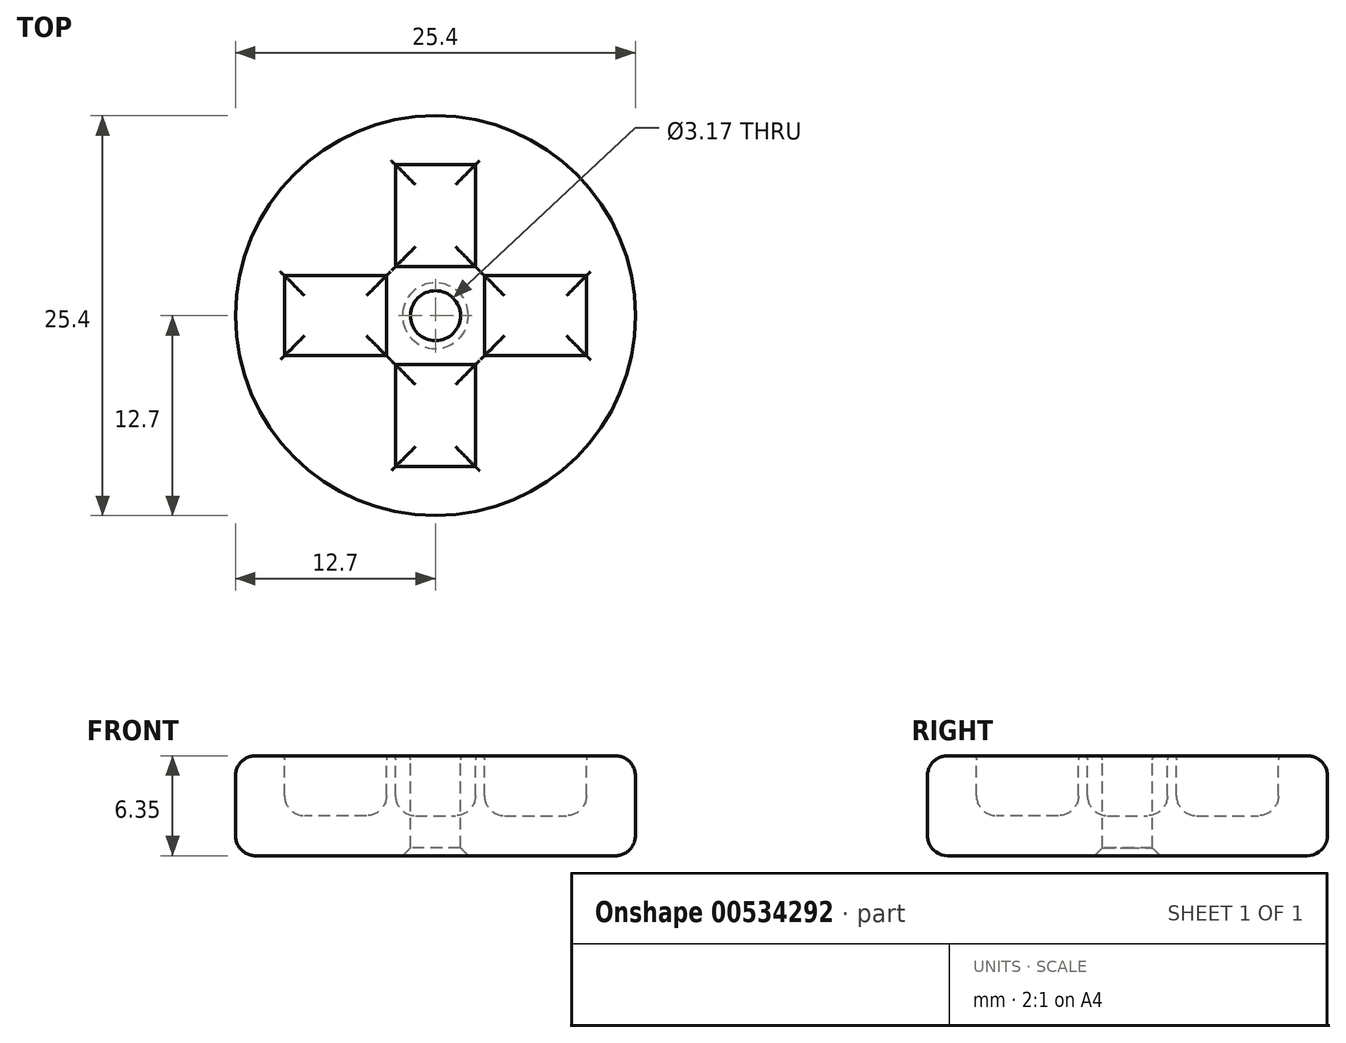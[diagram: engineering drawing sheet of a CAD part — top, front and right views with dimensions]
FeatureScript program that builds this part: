
annotation { "Feature Type Name" : "Feature", "Feature Type Description" : "" }
export const myFeature = defineFeature(function(context is Context, id is Id, definition is map)
    precondition{}
    {
        {
            var Q0;
            Q0=qCreatedBy(makeId("Top.planeOp"),FACE);
            var sketch = newSketch(context, id + "F0", { "sketchPlane" : qUnion([Q0])});
            skCircle(sketch, "E0", {"center": v(0, 0) * mm, "radius": 12.7 * mm});
            skSolve(sketch);
        }
        {
            var Q0;
            Q0 = qSketchRegion(id + "F0", true);
            extrude(context, id + "F1", {"entities" : qUnion([Q0]), "depth" : 6.35 * mm, "offsetDistance" : 25.4 * mm});
        }
        {
            var Q0;
            Q0=makeQuery(id+"F1.opExtrude","CAP_FACE",FACE,{"disambiguationData":[OSD([sQuery(id+"F0.wireOp",EDGE,"E0")])],"isStart":false});
            var sketch = newSketch(context, id + "F2", { "sketchPlane" : qUnion([Q0])});
            skCircle(sketch, "E1", {"center": v(0, 0) * mm, "radius": 1.59 * mm});
            skSolve(sketch);
        }
        {
            var Q0;
            Q0=makeQuery(id+"F2.imprint","IMPRINT",FACE,{"disambiguationData":[TD([[makeQuery(id+"F2.imprint","IMPRINT",EDGE,{"derivedFrom":sQuery(id+"F2.wireOp",EDGE,"E1")}),1.0]])]});
            extrude(context, id + "F3", {"entities" : qUnion([Q0]), "operationType" : NewBodyOperationType.REMOVE, "oppositeDirection" : true, "depth" : 25.4 * mm, "offsetDistance" : 25.4 * mm});
        }
        {
            var Q0;
            Q0=makeQuery(id+"F1.opExtrude","SWEPT_FACE",FACE,{"disambiguationData":[OSD([sQuery(id+"F0.wireOp",EDGE,"E0")])]});
            fillet(context, id + "F4", {"entities" : qUnion([Q0]), "radius" : 1.27 * mm, "tangentPropagation" : true, "allowEdgeOverflow" : false});
        }
        {
            var Q0;
            Q0=makeQuery(id+"F3.boolean.opBoolean","COPY",EDGE,{"derivedFrom":makeQuery(id+"F3.opExtrude","CAP_EDGE",EDGE,{"disambiguationData":[OSD([sQuery(id+"F2.wireOp",EDGE,"E1")])],"isStart":true})});
            var Q1;
            Q1=makeQuery(id+"F3.boolean.opBoolean","INTERSECT",EDGE,{"derivedFrom":[makeQuery(id+"F1.opExtrude","CAP_FACE",FACE,{"disambiguationData":[OSD([sQuery(id+"F0.wireOp",EDGE,"E0")])],"isStart":true}),makeQuery(id+"F3.opExtrude","SWEPT_FACE",FACE,{"disambiguationData":[OSD([sQuery(id+"F2.wireOp",EDGE,"E1")])]})]});
            chamfer(context, id + "F5", {"entities" : qUnion([Q0, Q1]), "width" : 0.5 * mm, "tangentPropagation" : true});
        }
        {
            var Q0;
            Q0=makeQuery(id+"F1.opExtrude","CAP_FACE",FACE,{"disambiguationData":[OSD([sQuery(id+"F0.wireOp",EDGE,"E0")])],"isStart":false});
            var sketch = newSketch(context, id + "F6", { "sketchPlane" : qUnion([Q0])});
            skLineSegment(sketch, "E2", {"start": v(0, 0) * mm, "end": v(0, 12.7) * mm});
            skLineSegment(sketch, "E3.bottom", {"start": v(2.54, 3.11) * mm, "end": v(-2.54, 3.11) * mm});
            skLineSegment(sketch, "E3.top", {"start": v(2.54, 9.59) * mm, "end": v(-2.54, 9.59) * mm});
            skLineSegment(sketch, "E3.left", {"start": v(2.54, 3.11) * mm, "end": v(2.54, 9.59) * mm});
            skLineSegment(sketch, "E3.right", {"start": v(-2.54, 3.11) * mm, "end": v(-2.54, 9.59) * mm});
            skPoint(sketch, "E3.middle", {"position": v(0, 6.35) * mm});
            skLineSegment(sketch, "E4.1.0", {"start": v(-9.59, 2.54) * mm, "end": v(-9.59, -2.54) * mm});
            skLineSegment(sketch, "E4.1.1", {"start": v(-3.11, -2.54) * mm, "end": v(-9.59, -2.54) * mm});
            skLineSegment(sketch, "E4.1.2", {"start": v(-3.11, 2.54) * mm, "end": v(-3.11, -2.54) * mm});
            skLineSegment(sketch, "E4.1.3", {"start": v(-3.11, 2.54) * mm, "end": v(-9.59, 2.54) * mm});
            skLineSegment(sketch, "E4.2.0", {"start": v(-2.54, -9.59) * mm, "end": v(2.54, -9.59) * mm});
            skLineSegment(sketch, "E4.2.1", {"start": v(2.54, -3.11) * mm, "end": v(2.54, -9.59) * mm});
            skLineSegment(sketch, "E4.2.2", {"start": v(-2.54, -3.11) * mm, "end": v(2.54, -3.11) * mm});
            skLineSegment(sketch, "E4.2.3", {"start": v(-2.54, -3.11) * mm, "end": v(-2.54, -9.59) * mm});
            skLineSegment(sketch, "E4.3.0", {"start": v(9.59, -2.54) * mm, "end": v(9.59, 2.54) * mm});
            skLineSegment(sketch, "E4.3.1", {"start": v(3.11, 2.54) * mm, "end": v(9.59, 2.54) * mm});
            skLineSegment(sketch, "E4.3.2", {"start": v(3.11, -2.54) * mm, "end": v(3.11, 2.54) * mm});
            skLineSegment(sketch, "E4.3.3", {"start": v(3.11, -2.54) * mm, "end": v(9.59, -2.54) * mm});
            skPoint(sketch, "E4.center", {"position": v(0, 0) * mm});
            skSolve(sketch);
        }
        {
            var Q0;
            {var subQ5=sQuery(id+"F6.wireOp",EDGE,"E3.right");Q0=makeQuery(id+"F6.imprint","IMPRINT",FACE,{"disambiguationData":[TD([[makeQuery(id+"F6.imprint","IMPRINT",EDGE,{"derivedFrom":subQ5}),-1.0]])]});}
            var Q1;
            {var subQ5=sQuery(id+"F6.wireOp",EDGE,"E3.left");Q1=makeQuery(id+"F6.imprint","IMPRINT",FACE,{"disambiguationData":[TD([[makeQuery(id+"F6.imprint","IMPRINT",EDGE,{"derivedFrom":subQ5}),1.0]])]});}
            var Q2;
            Q2=makeQuery(id+"F6.imprint","IMPRINT",FACE,{"disambiguationData":[TD([[makeQuery(id+"F6.imprint","IMPRINT",EDGE,{"derivedFrom":sQuery(id+"F6.wireOp",EDGE,"E4.1.0")}),1.0]])]});
            var Q3;
            Q3=makeQuery(id+"F6.imprint","IMPRINT",FACE,{"disambiguationData":[TD([[makeQuery(id+"F6.imprint","IMPRINT",EDGE,{"derivedFrom":sQuery(id+"F6.wireOp",EDGE,"E4.2.0")}),1.0]])]});
            var Q4;
            Q4=makeQuery(id+"F6.imprint","IMPRINT",FACE,{"disambiguationData":[TD([[makeQuery(id+"F6.imprint","IMPRINT",EDGE,{"derivedFrom":sQuery(id+"F6.wireOp",EDGE,"E4.3.0")}),1.0]])]});
            extrude(context, id + "F7", {"entities" : qUnion([Q0, Q1, Q2, Q3, Q4]), "operationType" : NewBodyOperationType.REMOVE, "oppositeDirection" : true, "depth" : 3.8 * mm, "offsetDistance" : 25.4 * mm});
        }
        {
            var Q0;
            Q0=makeQuery(id+"F7.boolean.opBoolean","COPY",FACE,{"derivedFrom":makeQuery(id+"F7.opExtrude","CAP_FACE",FACE,{"disambiguationData":[OSD([sQuery(id+"F6.wireOp",EDGE,"E4.2.0"),sQuery(id+"F6.wireOp",EDGE,"E4.2.1"),sQuery(id+"F6.wireOp",EDGE,"E4.2.2"),sQuery(id+"F6.wireOp",EDGE,"E4.2.3")])],"isStart":false})});
            var Q1;
            Q1=makeQuery(id+"F7.boolean.opBoolean","COPY",FACE,{"derivedFrom":makeQuery(id+"F7.opExtrude","CAP_FACE",FACE,{"disambiguationData":[OSD([sQuery(id+"F6.wireOp",EDGE,"E4.3.0"),sQuery(id+"F6.wireOp",EDGE,"E4.3.1"),sQuery(id+"F6.wireOp",EDGE,"E4.3.2"),sQuery(id+"F6.wireOp",EDGE,"E4.3.3")])],"isStart":false})});
            var Q2;
            Q2=makeQuery(id+"F7.boolean.opBoolean","COPY",FACE,{"derivedFrom":makeQuery(id+"F7.opExtrude","CAP_FACE",FACE,{"disambiguationData":[OSD([sQuery(id+"F6.wireOp",EDGE,"E4.1.0"),sQuery(id+"F6.wireOp",EDGE,"E4.1.1"),sQuery(id+"F6.wireOp",EDGE,"E4.1.2"),sQuery(id+"F6.wireOp",EDGE,"E4.1.3")])],"isStart":false})});
            var Q3;
            Q3=makeQuery(id+"F7.boolean.opBoolean","COPY",FACE,{"derivedFrom":makeQuery(id+"F7.opExtrude","CAP_FACE",FACE,{"disambiguationData":[OSD([sQuery(id+"F6.wireOp",EDGE,"E3.bottom"),sQuery(id+"F6.wireOp",EDGE,"E3.top"),sQuery(id+"F6.wireOp",EDGE,"E3.left"),sQuery(id+"F6.wireOp",EDGE,"E3.right")])],"isStart":false})});
            fillet(context, id + "F8", {"entities" : qUnion([Q0, Q1, Q2, Q3]), "radius" : 1.27 * mm, "tangentPropagation" : true, "allowEdgeOverflow" : false});
        }
        {
            var Q0;
            Q0=makeQuery(id+"F1.opExtrude","CAP_FACE",FACE,{"disambiguationData":[OSD([sQuery(id+"F0.wireOp",EDGE,"E0")])],"isStart":false});
            fillet(context, id + "F9", {"entities" : qUnion([Q0]), "radius" : 0.25 * mm, "tangentPropagation" : true, "allowEdgeOverflow" : false});
        }
    });
